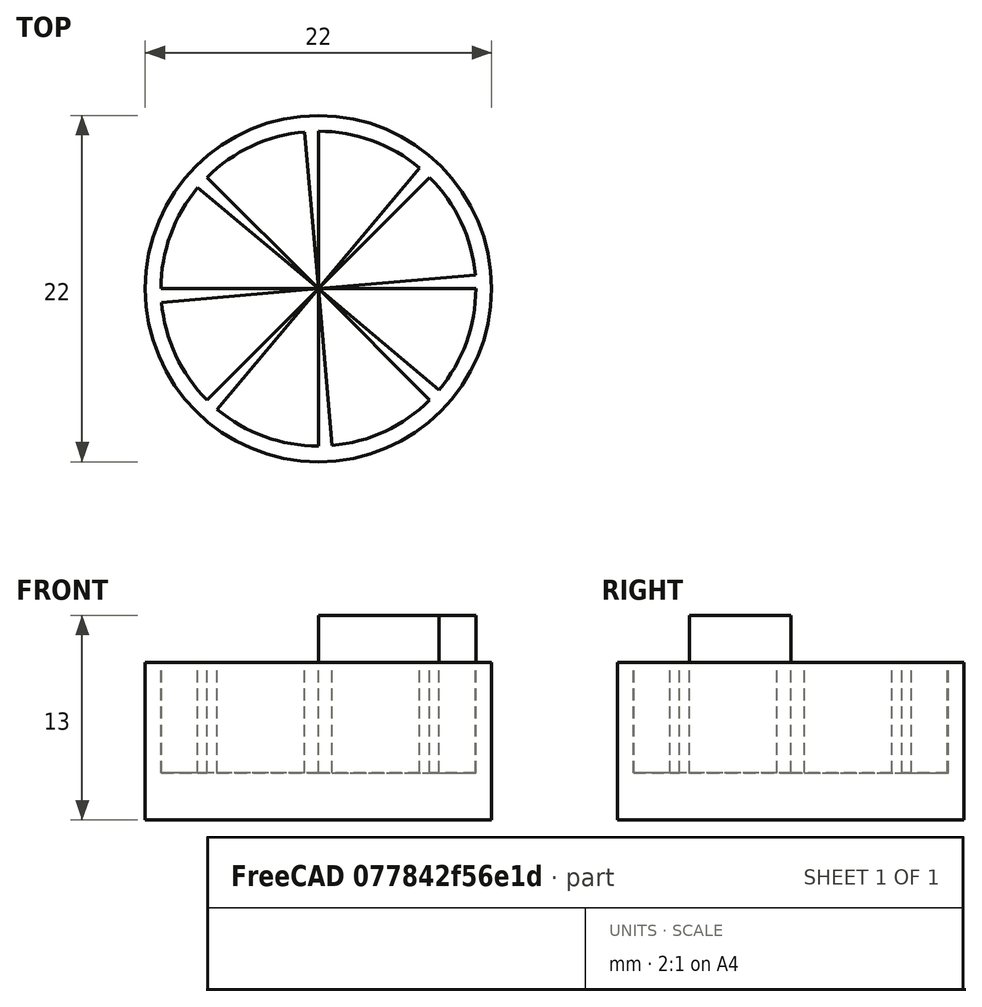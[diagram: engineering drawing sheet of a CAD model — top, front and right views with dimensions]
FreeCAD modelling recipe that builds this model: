
FCSTD DOCUMENT  (FreeCAD 0.20R29177 (Git))
Label: Ejercicio2Video11
License: All rights reserved
LicenseURL: http://en.wikipedia.org/wiki/All_rights_reserved
objects: Part::Cylinder×3, Part::Cut×2, Part::FeaturePython×1
note: 5 computed .brp shape members not serialized (recipe doc carries the construction recipe); baked Part::Feature solids carry a one-line shape summary decoded from their .brp

FEATURE [Part::Cylinder] Cylinder  label="Base"
  Angle = 360
  AttacherType = Attacher::AttachEngine3D
  FirstAngle = 0
  Height = 10
  Radius = 10
  SecondAngle = 0
FEATURE [Part::Cylinder] Cylinder001  label="Cilindro"
  Angle = 320
  AttacherType = Attacher::AttachEngine3D
  FirstAngle = 0
  Height = 10
  Radius = 10
  SecondAngle = 0
FEATURE [Part::Cut] Cut  label="Quesito"
  Base = -> Cylinder
  Placement = pos=(0,0,3) rot=(0,0,1;0rad)
  Tool = -> Cylinder001
FEATURE [Part::Cylinder] Cylinder002  label="Cilindro001"
  Angle = 360
  AttacherType = Attacher::AttachEngine3D
  FirstAngle = 0
  Height = 10
  Radius = 11
  SecondAngle = 0
FEATURE [Part::FeaturePython] Array  # Draft array (typed FeaturePython)
  AlwaysSyncPlacement = false
  Angle = 360
  ArrayType = 1
  Axis = (0,0,1)
  Base = -> Cut
  Center = (0,0,0)
  Count = 8
  ExpandArray = false
  Fuse = false
  IntervalAxis = (0,0,0)
  IntervalX = (100,0,0)
  IntervalY = (0,100,0)
  IntervalZ = (0,0,100)
  NumberCircles = 3
  NumberPolar = 8
  NumberX = 2
  NumberY = 2
  NumberZ = 1
  PlacementList = 8 placements: [(0,0,3),(0,0,3),(0,0,3),(0,0,3),(0,0,3),(0,0,3),(0,0,3),(0,0,3)]
  RadialDistance = 50
  ScaleList = (8) [(1,1,1),(1,1,1),(1,1,1),(1,1,1),(1,1,1),(1,1,1),(1,1,1),(1,1,1)]
  Symmetry = 1
  TangentialDistance = 25
FEATURE [Part::Cut] Cut001
  Base = -> Cylinder002
  Tool = -> Array
